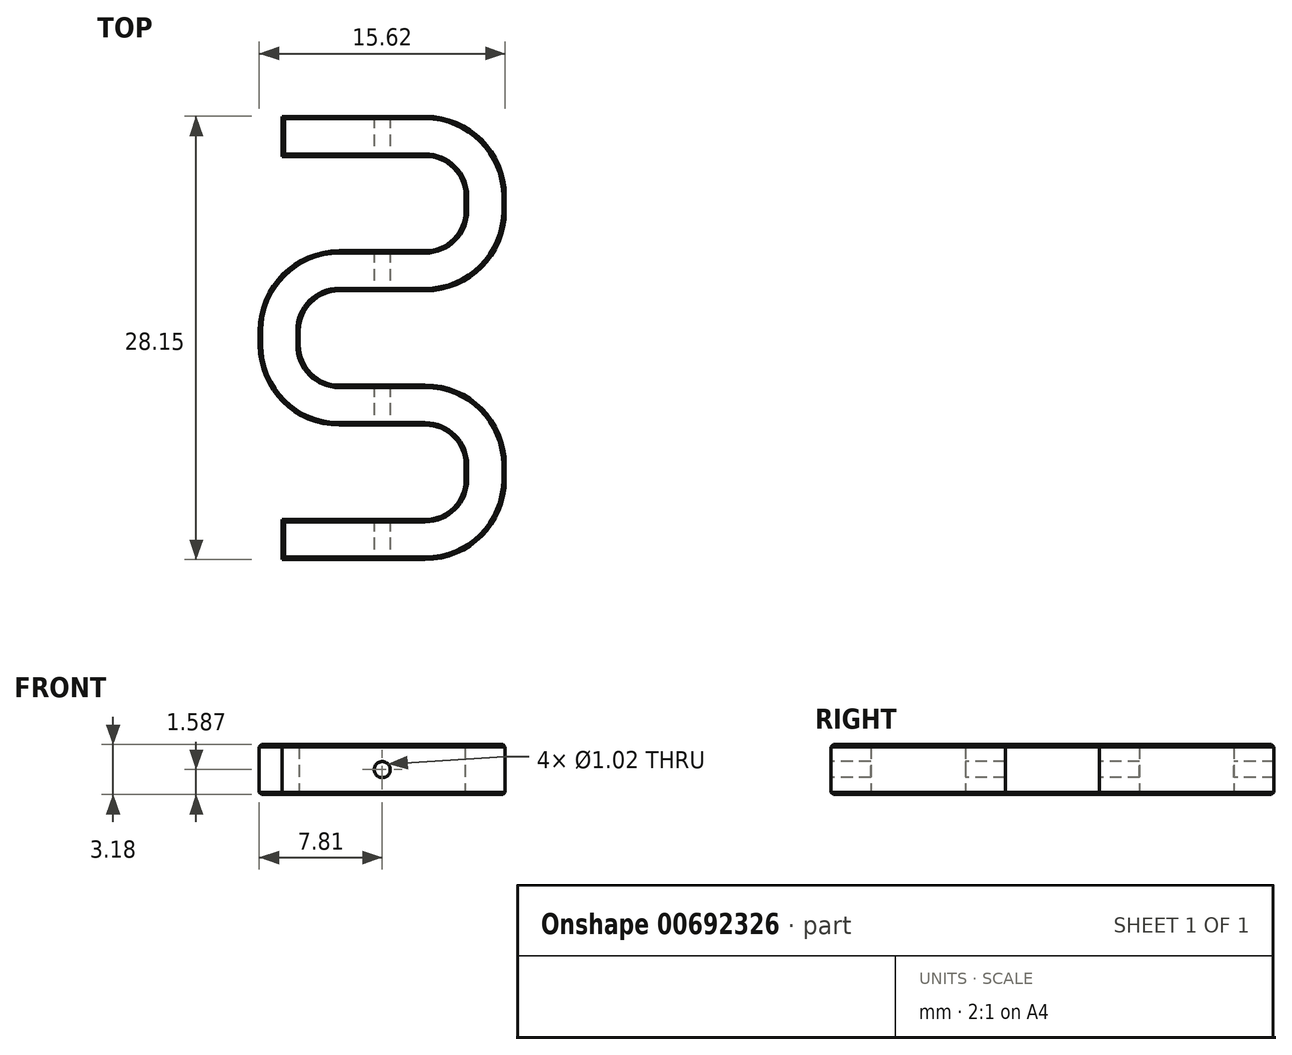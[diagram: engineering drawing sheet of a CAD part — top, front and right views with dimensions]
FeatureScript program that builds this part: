
annotation { "Feature Type Name" : "Feature", "Feature Type Description" : "" }
export const myFeature = defineFeature(function(context is Context, id is Id, definition is map)
    precondition{}
    {
        {
            var Q0;
            Q0=qCreatedBy(makeId("Top.planeOp"),FACE);
            var sketch = newSketch(context, id + "F0", { "sketchPlane" : qUnion([Q0])});
            skLineSegment(sketch, "E0.bottom", {"start": v(2.73, -3) * mm, "end": v(-2.73, -3) * mm});
            skLineSegment(sketch, "E0.top", {"start": v(2.73, 3) * mm, "end": v(-6.35, 3) * mm});
            skLineSegment(sketch, "E0.left", {"start": v(4, -0.08) * mm, "end": v(4, 0.08) * mm});
            skLineSegment(sketch, "E0.right", {"start": v(-4, -0.08) * mm, "end": v(-4, 0.08) * mm});
            skPoint(sketch, "E0.middle", {"position": v(0, 0) * mm});
            skPoint(sketch, "E1.visualSharp", {"position": v(-4, 3) * mm});
            skArc(sketch, "E1.filletArc", {"start": v(-1.08, 3) * mm, "mid": v(-3.14, 2.14) * mm, "end": v(-4, 0.08) * mm});
            skPoint(sketch, "E2.visualSharp", {"position": v(-4, -3) * mm});
            skArc(sketch, "E2.filletArc", {"start": v(-4, -0.08) * mm, "mid": v(-3.14, -2.14) * mm, "end": v(-1.08, -3) * mm});
            skPoint(sketch, "E3.visualSharp", {"position": v(4, 3) * mm});
            skArc(sketch, "E3.filletArc", {"start": v(4, 0.08) * mm, "mid": v(3.14, 2.14) * mm, "end": v(1.08, 3) * mm});
            skPoint(sketch, "E4.visualSharp", {"position": v(4, -3) * mm});
            skArc(sketch, "E4.filletArc", {"start": v(1.08, -3) * mm, "mid": v(3.14, -2.14) * mm, "end": v(4, -0.08) * mm});
            skLineSegment(sketch, "E5.0", {"start": v(2.73, 5.54) * mm, "end": v(-6.35, 5.54) * mm});
            skLineSegment(sketch, "E6.0", {"start": v(2.73, -5.54) * mm, "end": v(-2.73, -5.54) * mm});
            skLineSegment(sketch, "E7.0", {"start": v(5.27, -0.46) * mm, "end": v(5.27, 0.46) * mm});
            skLineSegment(sketch, "E8.0", {"start": v(7.81, -0.46) * mm, "end": v(7.81, 0.46) * mm});
            skPoint(sketch, "E9.visualSharp", {"position": v(7.81, 5.54) * mm});
            skArc(sketch, "E9.filletArc", {"start": v(7.81, 0.46) * mm, "mid": v(6.32, 4.05) * mm, "end": v(2.73, 5.54) * mm});
            skArc(sketch, "E10.filletArc", {"start": v(2.73, -5.54) * mm, "mid": v(6.32, -4.05) * mm, "end": v(7.81, -0.46) * mm});
            skPoint(sketch, "E11.startSnap0", {"position": v(0.83, 5.54) * mm});
            skPoint(sketch, "E11.startSnap1", {"position": v(0, 3) * mm});
            skPoint(sketch, "E12.orphan", {"position": v(-1.08, 5.54) * mm});
            skArc(sketch, "E13.filletArc", {"start": v(5.27, 0.46) * mm, "mid": v(4.53, 2.25) * mm, "end": v(2.73, 3) * mm});
            skArc(sketch, "E14.filletArc", {"start": v(2.73, -3) * mm, "mid": v(4.53, -2.25) * mm, "end": v(5.27, -0.46) * mm});
            skArc(sketch, "E15.MirrorCS", {"start": v(1.08, -5.54) * mm, "mid": v(3.14, -6.4) * mm, "end": v(4, -8.46) * mm});
            skArc(sketch, "E16.MirrorCS", {"start": v(4, -8.61) * mm, "mid": v(3.14, -10.68) * mm, "end": v(1.08, -11.53) * mm});
            skArc(sketch, "E17.MirrorCS", {"start": v(-4, -8.46) * mm, "mid": v(-3.14, -6.4) * mm, "end": v(-1.08, -5.54) * mm});
            skArc(sketch, "E18.MirrorCS", {"start": v(-1.08, -11.53) * mm, "mid": v(-3.14, -10.68) * mm, "end": v(-4, -8.61) * mm});
            skArc(sketch, "E19.MirrorCS", {"start": v(-7.81, -9) * mm, "mid": v(-6.32, -12.58) * mm, "end": v(-2.73, -14.07) * mm});
            skArc(sketch, "E20.MirrorCS", {"start": v(-2.73, -3) * mm, "mid": v(-6.32, -4.49) * mm, "end": v(-7.81, -8.08) * mm});
            skArc(sketch, "E21.MirrorCS", {"start": v(-2.73, -5.54) * mm, "mid": v(-4.53, -6.28) * mm, "end": v(-5.27, -8.08) * mm});
            skArc(sketch, "E22.MirrorCS", {"start": v(-5.27, -9) * mm, "mid": v(-4.53, -10.79) * mm, "end": v(-2.73, -11.53) * mm});
            skLineSegment(sketch, "E23", {"start": v(4, -8.46) * mm, "end": v(4, -8.61) * mm});
            skLineSegment(sketch, "E24", {"start": v(-2.73, -14.07) * mm, "end": v(2.73, -14.07) * mm});
            skLineSegment(sketch, "E25", {"start": v(-2.73, -11.53) * mm, "end": v(1.08, -11.53) * mm});
            skLineSegment(sketch, "E26", {"start": v(-7.81, -8.08) * mm, "end": v(-7.81, -9) * mm});
            skLineSegment(sketch, "E27", {"start": v(-5.27, -8.08) * mm, "end": v(-5.27, -9) * mm});
            skLineSegment(sketch, "E28", {"start": v(-4, -8.46) * mm, "end": v(-4, -8.61) * mm});
            skLineSegment(sketch, "E29", {"start": v(1.08, -11.53) * mm, "end": v(3.81, -11.53) * mm});
            skLineSegment(sketch, "E30.trimOffspring", {"start": v(3.81, -11.53) * mm, "end": v(3.81, -11.65) * mm});
            skPoint(sketch, "E31.orphan", {"position": v(3.81, -5.54) * mm});
            skArc(sketch, "E32.MirrorCS", {"start": v(2.73, -11.53) * mm, "mid": v(6.32, -13.02) * mm, "end": v(7.81, -16.61) * mm});
            skLineSegment(sketch, "E33.MirrorCS", {"start": v(7.81, -16.61) * mm, "end": v(7.81, -17.53) * mm});
            skArc(sketch, "E34.MirrorCS", {"start": v(7.81, -17.53) * mm, "mid": v(6.32, -21.12) * mm, "end": v(2.73, -22.6) * mm});
            skLineSegment(sketch, "E35.MirrorCS", {"start": v(2.73, -22.6) * mm, "end": v(-6.35, -22.6) * mm});
            skLineSegment(sketch, "E36.MirrorCS", {"start": v(2.73, -20.07) * mm, "end": v(-6.35, -20.07) * mm});
            skArc(sketch, "E37.MirrorCS", {"start": v(5.27, -17.53) * mm, "mid": v(4.53, -19.32) * mm, "end": v(2.73, -20.07) * mm});
            skArc(sketch, "E38.MirrorCS", {"start": v(2.73, -14.07) * mm, "mid": v(4.53, -14.82) * mm, "end": v(5.27, -16.61) * mm});
            skArc(sketch, "E39.MirrorCS", {"start": v(1.08, -14.07) * mm, "mid": v(3.14, -14.93) * mm, "end": v(4, -17) * mm});
            skArc(sketch, "E40.MirrorCS", {"start": v(4, -17.14) * mm, "mid": v(3.14, -19.21) * mm, "end": v(1.08, -20.07) * mm});
            skLineSegment(sketch, "E41.MirrorCS", {"start": v(4, -17) * mm, "end": v(4, -17.14) * mm});
            skLineSegment(sketch, "E42.MirrorCS", {"start": v(5.27, -16.61) * mm, "end": v(5.27, -17.53) * mm});
            skArc(sketch, "E43.MirrorCS", {"start": v(-1.08, -20.07) * mm, "mid": v(-3.14, -19.21) * mm, "end": v(-4, -17.14) * mm});
            skArc(sketch, "E44.MirrorCS", {"start": v(-4, -17) * mm, "mid": v(-3.14, -14.93) * mm, "end": v(-1.08, -14.07) * mm});
            skLineSegment(sketch, "E45", {"start": v(-4, -17) * mm, "end": v(-4, -17.14) * mm});
            skLineSegment(sketch, "E46.0", {"start": v(-6.35, 5.54) * mm, "end": v(-6.35, 3) * mm});
            skLineSegment(sketch, "E47.trimOffspring", {"start": v(-6.35, -20.07) * mm, "end": v(-6.35, -22.6) * mm});
            skSolve(sketch);
        }
        {
            var Q0;
            Q0=makeQuery(id+"F0.imprint","IMPRINT",FACE,{"disambiguationData":[TD([[makeQuery(id+"F0.imprint","IMPRINT",EDGE,{"derivedFrom":sQuery(id+"F0.wireOp",EDGE,"E5.0")}),1.0]])]});
            extrude(context, id + "F1", {"entities" : qUnion([Q0]), "depth" : 3.17 * mm, "offsetDistance" : 25.4 * mm});
        }
        {
            var Q0;
            Q0=qCreatedBy(makeId("Front.planeOp"),FACE);
            cPlane(context, id + "F2", {"entities" : qUnion([Q0]), "cplaneType" : CPlaneType.OFFSET, "offset" : 22.6 * mm, "width" : 152.4 * mm, "height" : 152.4 * mm});
        }
        {
            var Q0;
            Q0=qCreatedBy(id+"F2.planeOp",FACE);
            var sketch = newSketch(context, id + "F3", { "sketchPlane" : qUnion([Q0])});
            skLineSegment(sketch, "E48", {"start": v(0, 0) * mm, "end": v(0, 6.65) * mm});
            skLineSegment(sketch, "E49", {"start": v(0, 0) * mm, "end": v(-3.12, 0) * mm});
            skLineSegment(sketch, "E50.0", {"start": v(0, 1.59) * mm, "end": v(-3.12, 1.59) * mm});
            skCircle(sketch, "E51", {"center": v(0, 1.59) * mm, "radius": 0.54 * mm});
            skSolve(sketch);
        }
        {
            var Q0;
            Q0=sQuery(id+"F3.wireOp",VERTEX,"E51.center");
            var Q1;
            Q1=makeQuery(id+"F1.opExtrude","SWEPT_BODY",BODY,{"disambiguationData":[OSD([sQuery(id+"F0.wireOp",EDGE,"E0.top"),sQuery(id+"F0.wireOp",EDGE,"E5.0"),sQuery(id+"F0.wireOp",EDGE,"E7.0"),sQuery(id+"F0.wireOp",EDGE,"E8.0"),sQuery(id+"F0.wireOp",EDGE,"E9.filletArc"),sQuery(id+"F0.wireOp",EDGE,"E10.filletArc"),sQuery(id+"F0.wireOp",EDGE,"E13.filletArc"),sQuery(id+"F0.wireOp",EDGE,"E14.filletArc"),sQuery(id+"F0.wireOp",EDGE,"E6.0"),sQuery(id+"F0.wireOp",EDGE,"E0.bottom"),sQuery(id+"F0.wireOp",EDGE,"E19.MirrorCS"),sQuery(id+"F0.wireOp",EDGE,"E20.MirrorCS"),sQuery(id+"F0.wireOp",EDGE,"E21.MirrorCS"),sQuery(id+"F0.wireOp",EDGE,"E22.MirrorCS"),sQuery(id+"F0.wireOp",EDGE,"E24"),sQuery(id+"F0.wireOp",EDGE,"E25"),sQuery(id+"F0.wireOp",EDGE,"E26"),sQuery(id+"F0.wireOp",EDGE,"E27"),sQuery(id+"F0.wireOp",EDGE,"E29"),sQuery(id+"F0.wireOp",EDGE,"E32.MirrorCS"),sQuery(id+"F0.wireOp",EDGE,"E33.MirrorCS"),sQuery(id+"F0.wireOp",EDGE,"E34.MirrorCS"),sQuery(id+"F0.wireOp",EDGE,"E35.MirrorCS"),sQuery(id+"F0.wireOp",EDGE,"E36.MirrorCS"),sQuery(id+"F0.wireOp",EDGE,"E37.MirrorCS"),sQuery(id+"F0.wireOp",EDGE,"E38.MirrorCS"),sQuery(id+"F0.wireOp",EDGE,"E42.MirrorCS"),sQuery(id+"F0.wireOp",EDGE,"E46.0"),sQuery(id+"F0.wireOp",EDGE,"E47.trimOffspring")])]});
            hole(context, id + "F4", {"style" : HoleStyle.SIMPLE, "endStyle" : HoleEndStyle.THROUGH, "holeDiameter" : 1.02 * mm, "majorDiameter" : 6.35 * mm, "isTappedThrough" : true, "tappedDepth" : 12.7 * mm, "tapClearance" : 3, "locations" : qUnion([Q0]), "scope" : qUnion([Q1])});
        }
        {
            var Q0;
            Q0=makeQuery(id+"F1.opExtrude","CAP_FACE",FACE,{"disambiguationData":[OSD([sQuery(id+"F0.wireOp",EDGE,"E0.top"),sQuery(id+"F0.wireOp",EDGE,"E5.0"),sQuery(id+"F0.wireOp",EDGE,"E7.0"),sQuery(id+"F0.wireOp",EDGE,"E8.0"),sQuery(id+"F0.wireOp",EDGE,"E9.filletArc"),sQuery(id+"F0.wireOp",EDGE,"E10.filletArc"),sQuery(id+"F0.wireOp",EDGE,"E13.filletArc"),sQuery(id+"F0.wireOp",EDGE,"E14.filletArc"),sQuery(id+"F0.wireOp",EDGE,"E6.0"),sQuery(id+"F0.wireOp",EDGE,"E0.bottom"),sQuery(id+"F0.wireOp",EDGE,"E19.MirrorCS"),sQuery(id+"F0.wireOp",EDGE,"E20.MirrorCS"),sQuery(id+"F0.wireOp",EDGE,"E21.MirrorCS"),sQuery(id+"F0.wireOp",EDGE,"E22.MirrorCS"),sQuery(id+"F0.wireOp",EDGE,"E24"),sQuery(id+"F0.wireOp",EDGE,"E25"),sQuery(id+"F0.wireOp",EDGE,"E26"),sQuery(id+"F0.wireOp",EDGE,"E27"),sQuery(id+"F0.wireOp",EDGE,"E29"),sQuery(id+"F0.wireOp",EDGE,"E32.MirrorCS"),sQuery(id+"F0.wireOp",EDGE,"E33.MirrorCS"),sQuery(id+"F0.wireOp",EDGE,"E34.MirrorCS"),sQuery(id+"F0.wireOp",EDGE,"E35.MirrorCS"),sQuery(id+"F0.wireOp",EDGE,"E36.MirrorCS"),sQuery(id+"F0.wireOp",EDGE,"E37.MirrorCS"),sQuery(id+"F0.wireOp",EDGE,"E38.MirrorCS"),sQuery(id+"F0.wireOp",EDGE,"E42.MirrorCS"),sQuery(id+"F0.wireOp",EDGE,"E46.0"),sQuery(id+"F0.wireOp",EDGE,"E47.trimOffspring")])],"isStart":false});
            var Q1;
            Q1=makeQuery(id+"F1.opExtrude","CAP_FACE",FACE,{"disambiguationData":[OSD([sQuery(id+"F0.wireOp",EDGE,"E0.top"),sQuery(id+"F0.wireOp",EDGE,"E5.0"),sQuery(id+"F0.wireOp",EDGE,"E7.0"),sQuery(id+"F0.wireOp",EDGE,"E8.0"),sQuery(id+"F0.wireOp",EDGE,"E9.filletArc"),sQuery(id+"F0.wireOp",EDGE,"E10.filletArc"),sQuery(id+"F0.wireOp",EDGE,"E13.filletArc"),sQuery(id+"F0.wireOp",EDGE,"E14.filletArc"),sQuery(id+"F0.wireOp",EDGE,"E6.0"),sQuery(id+"F0.wireOp",EDGE,"E0.bottom"),sQuery(id+"F0.wireOp",EDGE,"E19.MirrorCS"),sQuery(id+"F0.wireOp",EDGE,"E20.MirrorCS"),sQuery(id+"F0.wireOp",EDGE,"E21.MirrorCS"),sQuery(id+"F0.wireOp",EDGE,"E22.MirrorCS"),sQuery(id+"F0.wireOp",EDGE,"E24"),sQuery(id+"F0.wireOp",EDGE,"E25"),sQuery(id+"F0.wireOp",EDGE,"E26"),sQuery(id+"F0.wireOp",EDGE,"E27"),sQuery(id+"F0.wireOp",EDGE,"E29"),sQuery(id+"F0.wireOp",EDGE,"E32.MirrorCS"),sQuery(id+"F0.wireOp",EDGE,"E33.MirrorCS"),sQuery(id+"F0.wireOp",EDGE,"E34.MirrorCS"),sQuery(id+"F0.wireOp",EDGE,"E35.MirrorCS"),sQuery(id+"F0.wireOp",EDGE,"E36.MirrorCS"),sQuery(id+"F0.wireOp",EDGE,"E37.MirrorCS"),sQuery(id+"F0.wireOp",EDGE,"E38.MirrorCS"),sQuery(id+"F0.wireOp",EDGE,"E42.MirrorCS"),sQuery(id+"F0.wireOp",EDGE,"E46.0"),sQuery(id+"F0.wireOp",EDGE,"E47.trimOffspring")])],"isStart":true});
            chamfer(context, id + "F5", {"entities" : qUnion([Q0, Q1]), "width" : 0.15 * mm, "tangentPropagation" : true});
        }
    });
